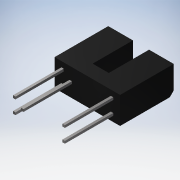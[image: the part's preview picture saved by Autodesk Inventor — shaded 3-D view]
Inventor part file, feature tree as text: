
AUTODESK INVENTOR PART (.ipt)
format: ipt  version: 2018.2 (Build 222227000, 227)  size: 139,776 bytes
history: native  units: mm
features: sketch x3, extrude x2, chamfer x1
ambient origin geometry x8: Origin, YZ Plane, XZ Plane, XY Plane, X Axis, Y Axis, Z Axis, Center Point
bodies: Solid1 (feature_tree)
feature tree (6):
  extrude  "Extrusion1"  Depth=10.0mm
  sketch  "Sketch2"  dims[d6=1.27mm d7=1.27mm d8=1.5mm d9=9.2mm d10=0.45mm d11=0.45mm d12=9.0mm d13=0.0mm d14=0.75mm d15=2.0mm d16=45.0deg]
  extrude  "Extrusion2"  Depth=3.0mm
  sketch  "Sketch Driven Pattern1"  dims[d0=12.2mm d1=10.0mm]
  chamfer  "Chamfer1"  Distance=5.0mm
  sketch  "Sketch1"  dims[d2=7.5mm d3=3.0mm d4=5.0mm d5=0.0mm]
